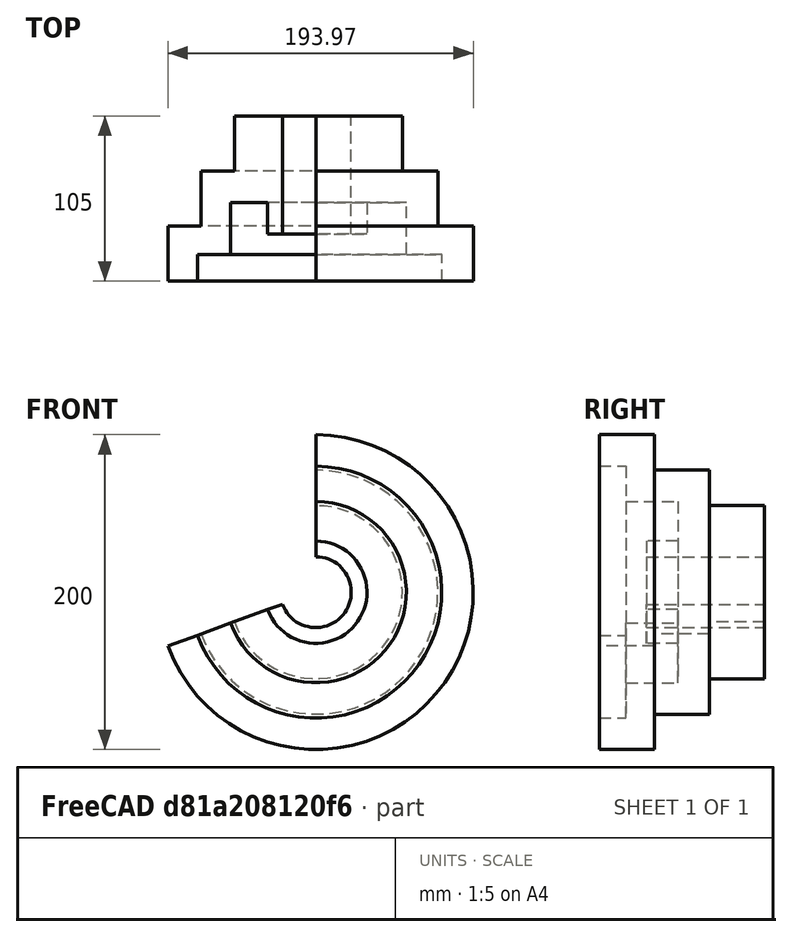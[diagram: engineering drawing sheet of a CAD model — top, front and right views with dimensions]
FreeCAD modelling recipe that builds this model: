
FCSTD DOCUMENT  (FreeCAD 0.16R)
Label: Ejer final 29
License: All rights reserved
LicenseURL: http://en.wikipedia.org/wiki/All_rights_reserved
objects: Sketcher::SketchObject×1, PartDesign::Revolution×1
note: 3 computed .brp shape members not serialized (recipe doc carries the construction recipe); baked Part::Feature solids carry a one-line shape summary decoded from their .brp

FEATURE [Sketcher::SketchObject] Sketch
  Placement = pos=(0,0,0) rot=(0.57735,0.57735,0.57735;2.0944rad)
  sketch-geometry (14):
    g0: LineSegment StartX=-75 StartY=22.5 StartZ=0 EndX=0 EndY=22.5 EndZ=0
    g1: LineSegment StartX=0 StartY=22.5 StartZ=0 EndX=0 EndY=55 EndZ=0
    g2: LineSegment StartX=0 StartY=55 StartZ=0 EndX=-35 EndY=55 EndZ=0
    g3: LineSegment StartX=-35 StartY=55 StartZ=0 EndX=-35 EndY=77.5 EndZ=0
    g4: LineSegment StartX=-35 StartY=77.5 StartZ=0 EndX=-70 EndY=77.5 EndZ=0
    g5: LineSegment StartX=-70 StartY=77.5 StartZ=0 EndX=-70 EndY=100 EndZ=0
    g6: LineSegment StartX=-70 StartY=100 StartZ=0 EndX=-105 EndY=100 EndZ=0
    g7: LineSegment StartX=-105 StartY=100 StartZ=0 EndX=-105 EndY=80 EndZ=0
    g8: LineSegment StartX=-105 StartY=80 StartZ=0 EndX=-88 EndY=80 EndZ=0
    g9: LineSegment StartX=-88 StartY=80 StartZ=0 EndX=-88 EndY=57.5 EndZ=0
    g10: LineSegment StartX=-88 StartY=57.5 StartZ=0 EndX=-55 EndY=57.5 EndZ=0
    g11: LineSegment StartX=-55 StartY=57.5 StartZ=0 EndX=-55 EndY=32.5 EndZ=0
    g12: LineSegment StartX=-55 StartY=32.5 StartZ=0 EndX=-75 EndY=32.5 EndZ=0
    g13: LineSegment StartX=-75 StartY=32.5 StartZ=0 EndX=-75 EndY=22.5 EndZ=0
  constraints (42):
    c: Horizontal(g0)
    c: Coincident(g0,g1)
    c: Coincident(g1,g2)
    c: Horizontal(g2)
    c: Coincident(g2,g3)
    c: Vertical(g3)
    c: Coincident(g3,g4)
    c: Horizontal(g4)
    c: Coincident(g4,g5)
    c: Vertical(g5)
    c: Coincident(g5,g6)
    c: Horizontal(g6)
    c: Coincident(g6,g7)
    c: Coincident(g7,g8)
    c: Horizontal(g8)
    c: Coincident(g8,g9)
    c: Vertical(g9)
    c: Coincident(g9,g10)
    c: Horizontal(g10)
    c: Coincident(g10,g11)
    c: Coincident(g11,g12)
    c: Coincident(g12,g13)
    c: Coincident(g13,g0)
    c: DistanceX(g0,g0) = 75
    c: Vertical(g13)
    c: Vertical(g1)
    c: Horizontal(g12)
    c: Vertical(g11)
    c: DistanceX(g6,g6) = 35
    c: DistanceX(g4,g4) = 35
    c: Vertical(g7)
    c: DistanceX(g2,g2) = 35
    c: DistanceX(g8,g8) = 17
    c: DistanceX(g10,g10) = 33
    c: DistanceY(g-1,g0) = 22.5
    c: DistanceY(g-1,g6) = 100
    c: DistanceY(g-1,g7) = 80
    c: DistanceY(g-1,g9) = 57.5
    c: DistanceY(g-1,g4) = 77.5
    c: DistanceY(g-1,g12) = 32.5
    c: DistanceY(g-1,g1) = 55
    c: DistanceX(g-1,g0) = 0
FEATURE [PartDesign::Revolution] Revolution
  Angle = 250
  Axis = (0,1,0)
  Base = (0,0,0)
  Placement = pos=(0,0,0) rot=(0.57735,0.57735,0.57735;2.0944rad)
  ReferenceAxis = -> Sketch [H_Axis]
  Sketch = -> Sketch
